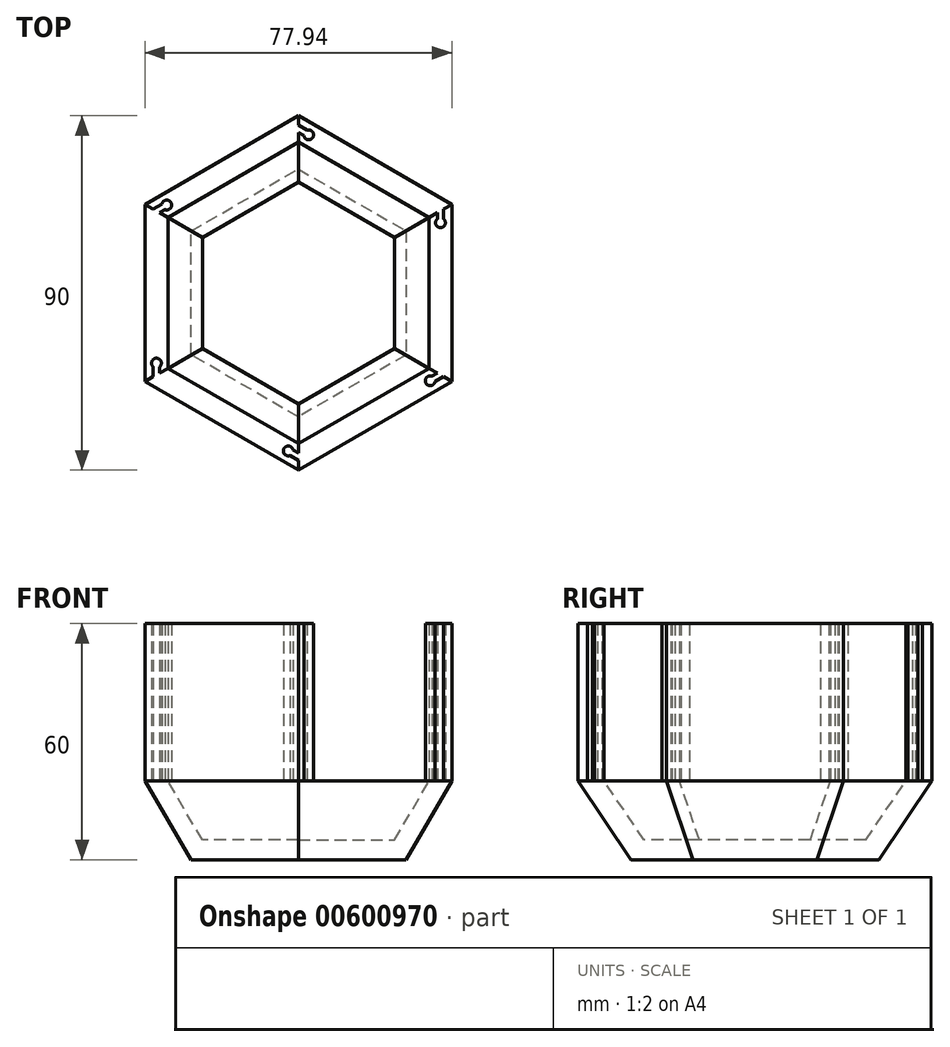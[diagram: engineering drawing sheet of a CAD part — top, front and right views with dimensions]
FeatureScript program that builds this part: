
annotation { "Feature Type Name" : "Feature", "Feature Type Description" : "" }
export const myFeature = defineFeature(function(context is Context, id is Id, definition is map)
    precondition{}
    {
        {
            var Q0;
            Q0=qCreatedBy(makeId("Top.planeOp"),FACE);
            var sketch = newSketch(context, id + "F0", { "sketchPlane" : qUnion([Q0])});
            skCircle(sketch, "E0.cCircle", {"center": v(0, 0) * mm, "radius": 31.5 * mm, "construction": true});
            skLineSegment(sketch, "E0.0", {"start": v(0, 31.5) * mm, "end": v(27.28, 15.75) * mm});
            skLineSegment(sketch, "E0.1", {"start": v(27.28, 15.75) * mm, "end": v(27.28, -15.75) * mm});
            skLineSegment(sketch, "E0.2", {"start": v(27.28, -15.75) * mm, "end": v(0, -31.5) * mm});
            skLineSegment(sketch, "E0.3", {"start": v(0, -31.5) * mm, "end": v(-27.28, -15.75) * mm});
            skLineSegment(sketch, "E0.4", {"start": v(-27.28, -15.75) * mm, "end": v(-27.28, 15.75) * mm});
            skLineSegment(sketch, "E0.5", {"start": v(-27.28, 15.75) * mm, "end": v(0, 31.5) * mm});
            skSolve(sketch);
        }
        {
            var Q0;
            Q0=makeQuery(id+"F0.imprint","IMPRINT",FACE,{"disambiguationData":[TD([[makeQuery(id+"F0.imprint","IMPRINT",EDGE,{"derivedFrom":sQuery(id+"F0.wireOp",EDGE,"E0.0")}),-1.0]])]});
            cPlane(context, id + "F1", {"entities" : qUnion([Q0]), "cplaneType" : CPlaneType.OFFSET, "offset" : 20 * mm, "width" : 150 * mm, "height" : 150 * mm});
        }
        {
            var Q0;
            Q0=qCreatedBy(id+"F1.planeOp",FACE);
            var sketch = newSketch(context, id + "F2", { "sketchPlane" : qUnion([Q0])});
            skCircle(sketch, "E1.cCircle", {"center": v(0, 0) * mm, "radius": 45 * mm, "construction": true});
            skLineSegment(sketch, "E1.0", {"start": v(0, -45) * mm, "end": v(-38.97, -22.5) * mm});
            skLineSegment(sketch, "E1.1", {"start": v(-38.97, -22.5) * mm, "end": v(-38.97, 22.5) * mm});
            skLineSegment(sketch, "E1.2", {"start": v(-38.97, 22.5) * mm, "end": v(0, 45) * mm});
            skLineSegment(sketch, "E1.3", {"start": v(0, 45) * mm, "end": v(38.97, 22.5) * mm});
            skLineSegment(sketch, "E1.4", {"start": v(38.97, 22.5) * mm, "end": v(38.97, -22.5) * mm});
            skLineSegment(sketch, "E1.5", {"start": v(38.97, -22.5) * mm, "end": v(0, -45) * mm});
            skSolve(sketch);
        }
        {
            var Q0;
            Q0=qCreatedBy(id+"F1.planeOp",FACE);
            cPlane(context, id + "F3", {"entities" : qUnion([Q0]), "cplaneType" : CPlaneType.OFFSET, "offset" : 40 * mm, "width" : 150 * mm, "height" : 150 * mm});
        }
        {
            var Q0;
            Q0=makeQuery(id+"F0.imprint","IMPRINT",FACE,{"disambiguationData":[TD([[makeQuery(id+"F0.imprint","IMPRINT",EDGE,{"derivedFrom":sQuery(id+"F0.wireOp",EDGE,"E0.0")}),-1.0]])]});
            var Q1;
            Q1=makeQuery(id+"F2.imprint","IMPRINT",FACE,{"disambiguationData":[TD([[makeQuery(id+"F2.imprint","IMPRINT",EDGE,{"derivedFrom":sQuery(id+"F2.wireOp",EDGE,"E1.0")}),-1.0]])]});
            loft(context, id + "F4", {"sheetProfilesArray" : [{ "sheetProfileEntities" : qUnion([Q0]) }, { "sheetProfileEntities" : qUnion([Q1]) }]});
        }
        {
            var Q0;
            Q0=makeQuery(id+"F4.opLoft","CAP_FACE",FACE,{"disambiguationData":[OSD([makeQuery(id+"F2.imprint","IMPRINT",FACE,{"disambiguationData":[TD([[makeQuery(id+"F2.imprint","IMPRINT",EDGE,{"derivedFrom":sQuery(id+"F2.wireOp",EDGE,"E1.0")}),-1.0]])]})])],"isStart":true});
            shell(context, id + "F5", {"entities" : qUnion([Q0]), "thickness" : 5 * mm});
        }
        {
            var Q0;
            Q0=makeQuery(id+"F4.opLoft","CAP_FACE",FACE,{"disambiguationData":[OSD([makeQuery(id+"F2.imprint","IMPRINT",FACE,{"disambiguationData":[TD([[makeQuery(id+"F2.imprint","IMPRINT",EDGE,{"derivedFrom":sQuery(id+"F2.wireOp",EDGE,"E1.0")}),-1.0]])]})])],"isStart":true});
            var sketch = newSketch(context, id + "F6", { "sketchPlane" : qUnion([Q0])});
            skLineSegment(sketch, "E2", {"start": v(-33.18, -19.16) * mm, "end": v(-33.18, 19.16) * mm});
            skLineSegment(sketch, "E3", {"start": v(-33.18, 19.16) * mm, "end": v(-35.28, 20.37) * mm});
            skLineSegment(sketch, "E4", {"start": v(-38.97, 22.5) * mm, "end": v(-38.97, -22.5) * mm});
            skLineSegment(sketch, "E5", {"start": v(-36.08, 20.83) * mm, "end": v(0, 41.66) * mm, "construction": true});
            skArc(sketch, "E6", {"start": v(-33.9, 21.16) * mm, "mid": v(-32.4, 22.95) * mm, "end": v(-34.7, 22.54) * mm});
            skLineSegment(sketch, "E7", {"start": v(-36.88, 21.29) * mm, "end": v(-34.7, 22.54) * mm});
            skLineSegment(sketch, "E8", {"start": v(-35.28, 20.37) * mm, "end": v(-33.9, 21.16) * mm});
            skLineSegment(sketch, "E9", {"start": v(-38.97, -22.5) * mm, "end": v(-36.88, -21.29) * mm});
            skLineSegment(sketch, "E10.1.0", {"start": v(-35.28, -20.37) * mm, "end": v(-35.28, -18.79) * mm});
            skArc(sketch, "E10.1.1", {"start": v(-35.28, -18.79) * mm, "mid": v(-36.08, -16.58) * mm, "end": v(-36.88, -18.79) * mm});
            skLineSegment(sketch, "E10.1.2", {"start": v(-36.88, -21.29) * mm, "end": v(-36.88, -18.79) * mm});
            skLineSegment(sketch, "E11", {"start": v(-36.08, -20.83) * mm, "end": v(-36.08, 20.83) * mm, "construction": true});
            skLineSegment(sketch, "E12.trimOffspring", {"start": v(-35.28, -20.37) * mm, "end": v(-33.18, -19.16) * mm});
            skLineSegment(sketch, "E13.trimOffspring", {"start": v(-36.88, 21.29) * mm, "end": v(-38.97, 22.5) * mm});
            skLineSegment(sketch, "E14.1.0", {"start": v(0, -41.66) * mm, "end": v(-36.08, -20.83) * mm, "construction": true});
            skLineSegment(sketch, "E14.1.1", {"start": v(-38.97, -22.5) * mm, "end": v(0, -45) * mm});
            skLineSegment(sketch, "E14.1.2", {"start": v(0, -38.31) * mm, "end": v(-33.18, -19.16) * mm});
            skArc(sketch, "E14.1.3", {"start": v(-1.37, -39.94) * mm, "mid": v(-3.68, -39.53) * mm, "end": v(-2.17, -41.33) * mm});
            skLineSegment(sketch, "E14.1.4", {"start": v(-33.18, -19.16) * mm, "end": v(-35.28, -20.37) * mm});
            skLineSegment(sketch, "E14.1.6", {"start": v(0, -40.73) * mm, "end": v(0, -38.31) * mm});
            skLineSegment(sketch, "E14.1.7", {"start": v(0, -45) * mm, "end": v(0, -42.58) * mm});
            skLineSegment(sketch, "E14.1.10", {"start": v(-36.88, -21.29) * mm, "end": v(-38.97, -22.5) * mm});
            skLineSegment(sketch, "E14.1.11", {"start": v(0, -42.58) * mm, "end": v(-2.17, -41.33) * mm});
            skLineSegment(sketch, "E14.1.12", {"start": v(0, -40.73) * mm, "end": v(-1.37, -39.94) * mm});
            skLineSegment(sketch, "E14.2.0", {"start": v(36.08, -20.83) * mm, "end": v(0, -41.66) * mm, "construction": true});
            skLineSegment(sketch, "E14.2.1", {"start": v(0, -45) * mm, "end": v(38.97, -22.5) * mm});
            skLineSegment(sketch, "E14.2.2", {"start": v(33.18, -19.16) * mm, "end": v(0, -38.31) * mm});
            skArc(sketch, "E14.2.3", {"start": v(33.9, -21.16) * mm, "mid": v(32.4, -22.95) * mm, "end": v(34.7, -22.54) * mm});
            skLineSegment(sketch, "E14.2.4", {"start": v(0, -38.31) * mm, "end": v(0, -40.73) * mm});
            skArc(sketch, "E14.2.5", {"start": v(-1.37, -39.94) * mm, "mid": v(-3.68, -39.53) * mm, "end": v(-2.17, -41.33) * mm});
            skLineSegment(sketch, "E14.2.6", {"start": v(35.28, -20.37) * mm, "end": v(33.18, -19.16) * mm});
            skLineSegment(sketch, "E14.2.7", {"start": v(38.97, -22.5) * mm, "end": v(36.88, -21.29) * mm});
            skLineSegment(sketch, "E14.2.8", {"start": v(0, -42.58) * mm, "end": v(-2.17, -41.33) * mm});
            skLineSegment(sketch, "E14.2.9", {"start": v(0, -40.73) * mm, "end": v(-1.37, -39.94) * mm});
            skLineSegment(sketch, "E14.2.10", {"start": v(0, -42.58) * mm, "end": v(0, -45) * mm});
            skLineSegment(sketch, "E14.2.11", {"start": v(36.88, -21.29) * mm, "end": v(34.7, -22.54) * mm});
            skLineSegment(sketch, "E14.2.12", {"start": v(35.28, -20.37) * mm, "end": v(33.9, -21.16) * mm});
            skLineSegment(sketch, "E14.3.0", {"start": v(36.08, 20.83) * mm, "end": v(36.08, -20.83) * mm, "construction": true});
            skLineSegment(sketch, "E14.3.1", {"start": v(38.97, -22.5) * mm, "end": v(38.97, 22.5) * mm});
            skLineSegment(sketch, "E14.3.2", {"start": v(33.18, 19.16) * mm, "end": v(33.18, -19.16) * mm});
            skArc(sketch, "E14.3.3", {"start": v(35.28, 18.79) * mm, "mid": v(36.08, 16.58) * mm, "end": v(36.88, 18.79) * mm});
            skLineSegment(sketch, "E14.3.4", {"start": v(33.18, -19.16) * mm, "end": v(35.28, -20.37) * mm});
            skArc(sketch, "E14.3.5", {"start": v(33.9, -21.16) * mm, "mid": v(32.4, -22.95) * mm, "end": v(34.7, -22.54) * mm});
            skLineSegment(sketch, "E14.3.6", {"start": v(35.28, 20.37) * mm, "end": v(33.18, 19.16) * mm});
            skLineSegment(sketch, "E14.3.7", {"start": v(38.97, 22.5) * mm, "end": v(36.88, 21.29) * mm});
            skLineSegment(sketch, "E14.3.8", {"start": v(36.88, -21.29) * mm, "end": v(34.7, -22.54) * mm});
            skLineSegment(sketch, "E14.3.9", {"start": v(35.28, -20.37) * mm, "end": v(33.9, -21.16) * mm});
            skLineSegment(sketch, "E14.3.10", {"start": v(36.88, -21.29) * mm, "end": v(38.97, -22.5) * mm});
            skLineSegment(sketch, "E14.3.11", {"start": v(36.88, 21.29) * mm, "end": v(36.88, 18.79) * mm});
            skLineSegment(sketch, "E14.3.12", {"start": v(35.28, 20.37) * mm, "end": v(35.28, 18.79) * mm});
            skLineSegment(sketch, "E14.4.0", {"start": v(0, 41.66) * mm, "end": v(36.08, 20.83) * mm, "construction": true});
            skLineSegment(sketch, "E14.4.1", {"start": v(38.97, 22.5) * mm, "end": v(0, 45) * mm});
            skLineSegment(sketch, "E14.4.2", {"start": v(0, 38.31) * mm, "end": v(33.18, 19.16) * mm});
            skArc(sketch, "E14.4.3", {"start": v(1.37, 39.94) * mm, "mid": v(3.68, 39.53) * mm, "end": v(2.17, 41.33) * mm});
            skLineSegment(sketch, "E14.4.4", {"start": v(33.18, 19.16) * mm, "end": v(35.28, 20.37) * mm});
            skArc(sketch, "E14.4.5", {"start": v(35.28, 18.79) * mm, "mid": v(36.08, 16.58) * mm, "end": v(36.88, 18.79) * mm});
            skLineSegment(sketch, "E14.4.6", {"start": v(0, 40.73) * mm, "end": v(0, 38.31) * mm});
            skLineSegment(sketch, "E14.4.7", {"start": v(0, 45) * mm, "end": v(0, 42.58) * mm});
            skLineSegment(sketch, "E14.4.8", {"start": v(36.88, 21.29) * mm, "end": v(36.88, 18.79) * mm});
            skLineSegment(sketch, "E14.4.9", {"start": v(35.28, 20.37) * mm, "end": v(35.28, 18.79) * mm});
            skLineSegment(sketch, "E14.4.10", {"start": v(36.88, 21.29) * mm, "end": v(38.97, 22.5) * mm});
            skLineSegment(sketch, "E14.4.11", {"start": v(0, 42.58) * mm, "end": v(2.17, 41.33) * mm});
            skLineSegment(sketch, "E14.4.12", {"start": v(0, 40.73) * mm, "end": v(1.37, 39.94) * mm});
            skLineSegment(sketch, "E14.5.1", {"start": v(0, 45) * mm, "end": v(-38.97, 22.5) * mm});
            skLineSegment(sketch, "E14.5.2", {"start": v(-33.18, 19.16) * mm, "end": v(0, 38.31) * mm});
            skLineSegment(sketch, "E14.5.4", {"start": v(0, 38.31) * mm, "end": v(0, 40.73) * mm});
            skArc(sketch, "E14.5.5", {"start": v(1.37, 39.94) * mm, "mid": v(3.68, 39.53) * mm, "end": v(2.17, 41.33) * mm});
            skLineSegment(sketch, "E14.5.6", {"start": v(-35.28, 20.37) * mm, "end": v(-33.18, 19.16) * mm});
            skLineSegment(sketch, "E14.5.7", {"start": v(-38.97, 22.5) * mm, "end": v(-36.88, 21.29) * mm});
            skLineSegment(sketch, "E14.5.8", {"start": v(0, 42.58) * mm, "end": v(2.17, 41.33) * mm});
            skLineSegment(sketch, "E14.5.9", {"start": v(0, 40.73) * mm, "end": v(1.37, 39.94) * mm});
            skLineSegment(sketch, "E14.5.10", {"start": v(0, 42.58) * mm, "end": v(0, 45) * mm});
            skPoint(sketch, "E14.center", {"position": v(0, 0) * mm});
            skSolve(sketch);
        }
        {
            var Q0;
            Q0=makeQuery(id+"F6.imprint","IMPRINT",FACE,{"disambiguationData":[TD([[makeQuery(id+"F6.imprint","IMPRINT",EDGE,{"derivedFrom":sQuery(id+"F6.wireOp",EDGE,"E14.1.1")}),1.0]])]});
            var Q1;
            Q1=makeQuery(id+"F6.imprint","IMPRINT",FACE,{"disambiguationData":[TD([[makeQuery(id+"F6.imprint","IMPRINT",EDGE,{"derivedFrom":sQuery(id+"F6.wireOp",EDGE,"E14.5.1")}),1.0]])]});
            var Q2;
            Q2=makeQuery(id+"F6.imprint","IMPRINT",FACE,{"disambiguationData":[TD([[makeQuery(id+"F6.imprint","IMPRINT",EDGE,{"derivedFrom":sQuery(id+"F6.wireOp",EDGE,"E14.3.1")}),1.0]])]});
            extrude(context, id + "F7", {"entities" : qUnion([Q0, Q1, Q2]), "operationType" : NewBodyOperationType.ADD, "depth" : 40 * mm, "offsetDistance" : 25 * mm});
        }
    });
